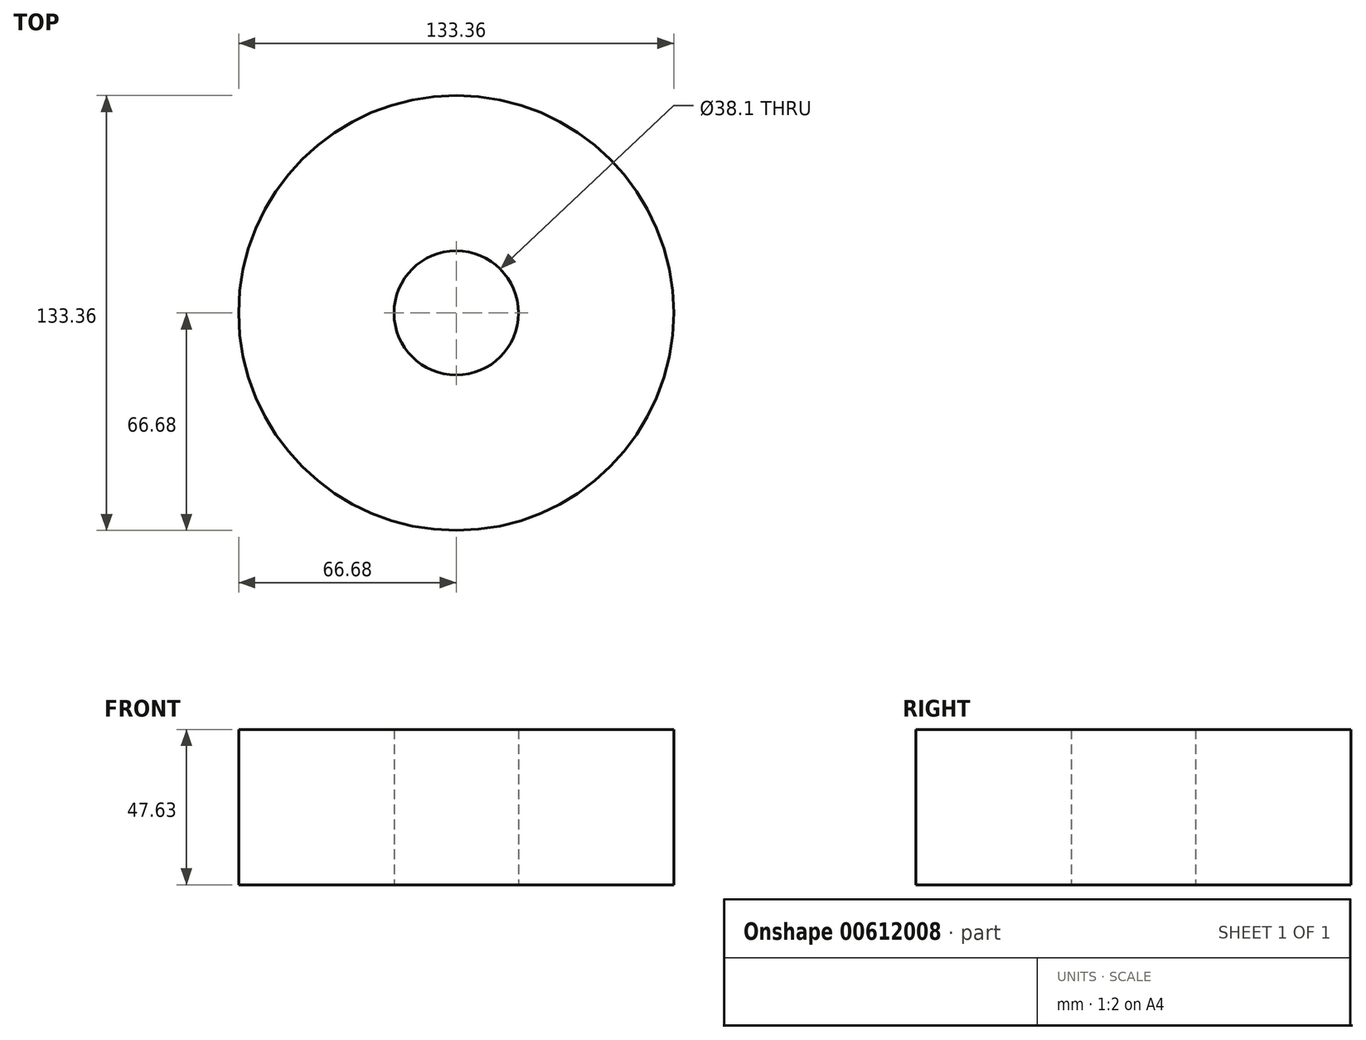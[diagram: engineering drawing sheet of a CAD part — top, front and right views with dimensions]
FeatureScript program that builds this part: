
annotation { "Feature Type Name" : "Feature", "Feature Type Description" : "" }
export const myFeature = defineFeature(function(context is Context, id is Id, definition is map)
    precondition{}
    {
        {
            var Q0;
            Q0=qCreatedBy(makeId("Top.planeOp"),FACE);
            var sketch = newSketch(context, id + "F0", { "sketchPlane" : qUnion([Q0])});
            skCircle(sketch, "E0", {"center": v(0, 0) * mm, "radius": 66.67 * mm});
            skCircle(sketch, "E1", {"center": v(0, 0) * mm, "radius": 19.05 * mm});
            skPoint(sketch, "E2.center.orphan", {"position": v(-49.33, 0) * mm});
            skSolve(sketch);
        }
        {
            var Q0;
            Q0 = qSketchRegion(id + "F0", true);
            extrude(context, id + "F1", {"entities" : qUnion([Q0]), "depth" : 47.62 * mm, "offsetDistance" : 25 * mm});
        }
    });
